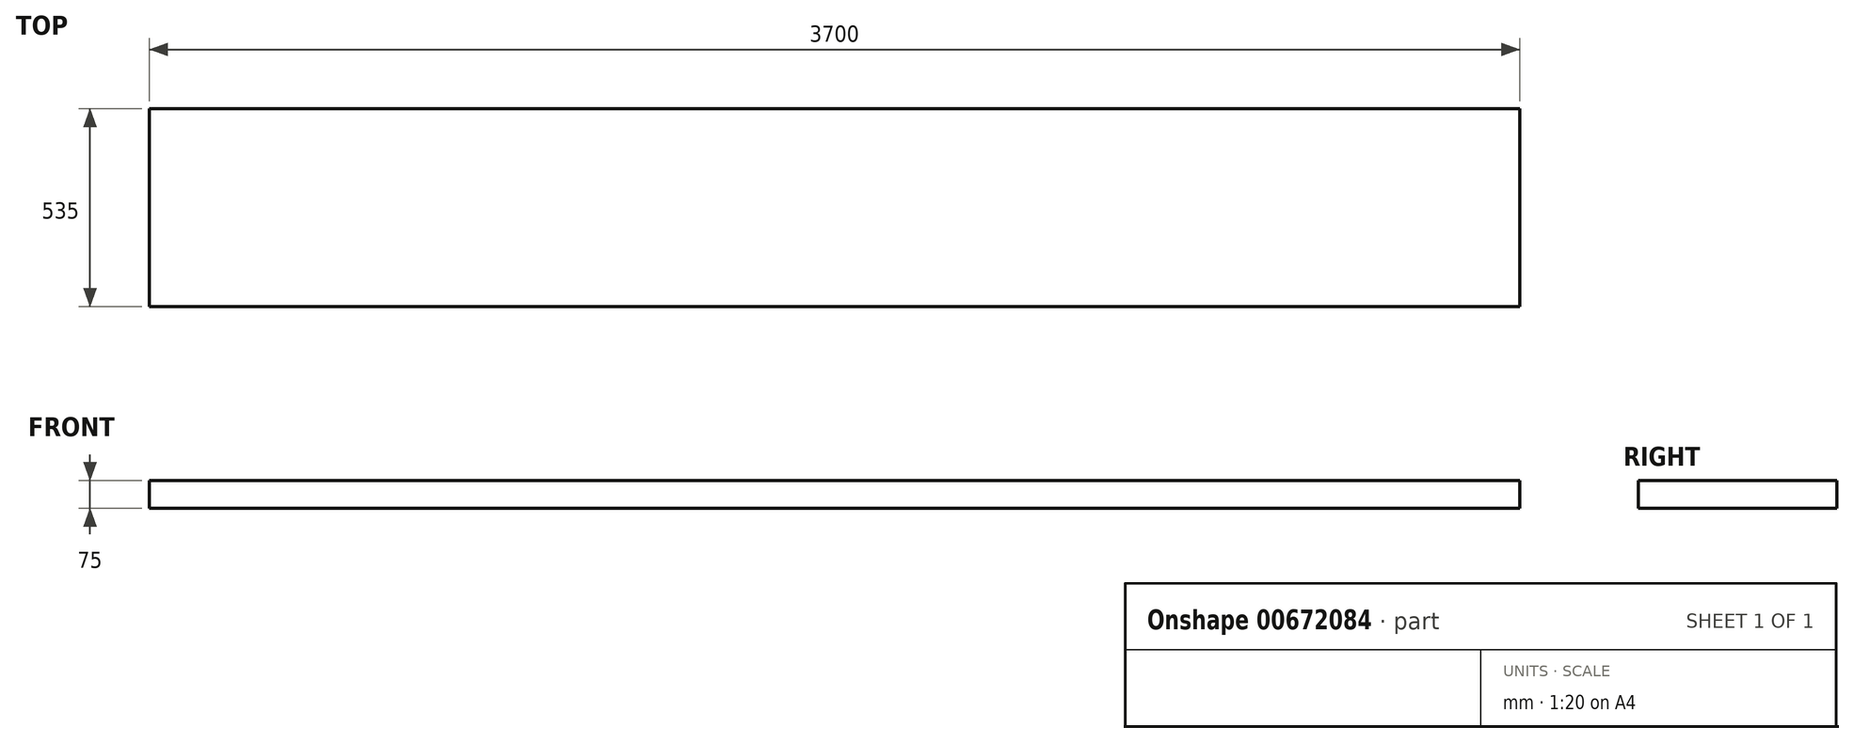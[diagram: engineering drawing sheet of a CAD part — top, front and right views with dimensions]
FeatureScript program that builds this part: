
annotation { "Feature Type Name" : "Feature", "Feature Type Description" : "" }
export const myFeature = defineFeature(function(context is Context, id is Id, definition is map)
    precondition{}
    {
        {
            var Q0;
            Q0=qCreatedBy(makeId("Top.planeOp"),FACE);
            var sketch = newSketch(context, id + "F0", { "sketchPlane" : qUnion([Q0])});
            skLineSegment(sketch, "E0.bottom", {"start": v(420.06, -280.3) * mm, "end": v(-3279.94, -280.3) * mm});
            skLineSegment(sketch, "E0.top", {"start": v(420.06, 254.7) * mm, "end": v(-3279.94, 254.7) * mm});
            skLineSegment(sketch, "E0.left", {"start": v(420.06, -280.3) * mm, "end": v(420.06, 254.7) * mm});
            skLineSegment(sketch, "E0.right", {"start": v(-3279.94, -280.3) * mm, "end": v(-3279.94, 254.7) * mm});
            skPoint(sketch, "E0.middle", {"position": v(-1429.94, -12.8) * mm});
            skSolve(sketch);
        }
        {
            var Q0;
            Q0 = qSketchRegion(id + "F0", true);
            extrude(context, id + "F1", {"entities" : qUnion([Q0]), "depth" : 75 * mm, "offsetDistance" : 25 * mm});
        }
    });
